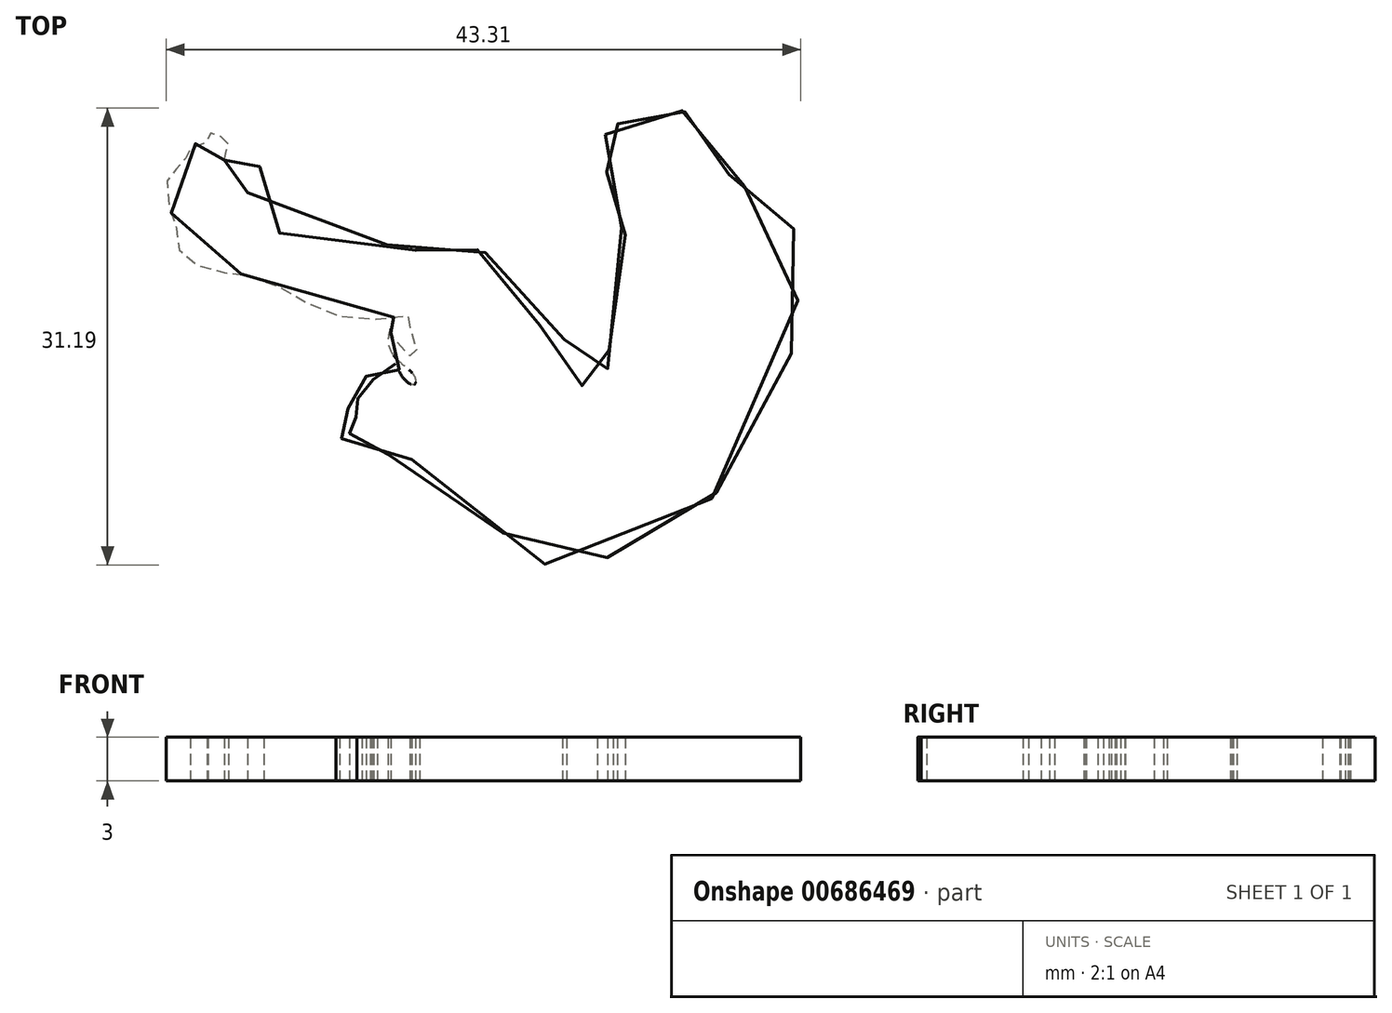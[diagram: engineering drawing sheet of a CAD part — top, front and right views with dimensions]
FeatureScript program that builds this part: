
annotation { "Feature Type Name" : "Feature", "Feature Type Description" : "" }
export const myFeature = defineFeature(function(context is Context, id is Id, definition is map)
    precondition{}
    {
        {
            var Q0;
            Q0=qCreatedBy(makeId("Top.planeOp"),FACE);
            var sketch = newSketch(context, id + "F0", { "sketchPlane" : qUnion([Q0])});
            skFitSpline(sketch, "E0", {"points": [v(-54, 35.11) * mm, v(-53.98, 35.18) * mm, v(-53.72, 36.26) * mm, v(-53.86, 36.83) * mm, v(-54.43, 36.67) * mm, v(-54.64, 36.97) * mm, v(-55.17, 36.79) * mm, v(-55.12, 36.37) * mm, v(-55.79, 36.33) * mm, v(-56.3, 35.82) * mm, v(-56.31, 35.57) * mm, v(-56.75, 35.18) * mm, v(-57.23, 34.63) * mm, v(-57.37, 34.34) * mm, v(-57.83, 33.88) * mm, v(-57.78, 31.98) * mm, v(-57.28, 30.6) * mm, v(-57.16, 29.25) * mm, v(-56.34, 28.2) * mm, v(-54.1, 27.46) * mm, v(-53.04, 27.37) * mm, v(-49.83, 26.27) * mm, v(-47.22, 24.8) * mm, v(-43.37, 24.28) * mm, v(-41.24, 24.44) * mm, v(-41.28, 23.91) * mm, v(-41.08, 22.51) * mm, v(-40.69, 21.67) * mm, v(-42.4, 22.51) * mm, v(-42.63, 23.61) * mm, v(-42.8, 22.6) * mm, v(-41.83, 21.18) * mm, v(-41, 20.34) * mm, v(-41.03, 19.79) * mm, v(-42, 20.59) * mm, v(-42.18, 21.32) * mm, v(-42.73, 21.02) * mm, v(-43.85, 21.57) * mm, v(-43.55, 20.68) * mm, v(-43.94, 20.95) * mm, v(-43.8, 20.2) * mm, v(-44.23, 20.33) * mm, v(-45.42, 20.45) * mm, v(-44.9, 19.52) * mm, v(-44.3, 18.99) * mm, v(-44.7, 18.84) * mm, v(-46.12, 18.91) * mm, v(-45.67, 18.3) * mm, v(-45.24, 17.97) * mm, v(-44.6, 17.86) * mm, v(-44.85, 17.66) * mm, v(-45.22, 17.39) * mm, v(-45.77, 16.81) * mm, v(-46.09, 16.8) * mm, v(-46.37, 16.42) * mm, v(-46.2, 15.89) * mm, v(-45.52, 16.46) * mm, v(-44.02, 15.62) * mm, v(-44.26, 15.42) * mm, v(-44.92, 14.7) * mm, v(-43.05, 15.02) * mm, v(-40.02, 13.98) * mm, v(-35.1, 9.77) * mm, v(-33.36, 8.2) * mm, v(-31.76, 7.49) * mm, v(-26.23, 8.02) * mm, v(-25.52, 7.7) * mm, v(-20.07, 12.82) * mm, v(-16.12, 19.16) * mm, v(-15.06, 23.56) * mm, v(-14.67, 29.52) * mm, v(-14.9, 30.13) * mm, v(-16.37, 31.9) * mm, v(-18.02, 33.26) * mm, v(-19.33, 33.64) * mm, v(-19.64, 35.14) * mm, v(-19.99, 36.5) * mm, v(-21.42, 37.92) * mm, v(-22.73, 38.5) * mm, v(-22.96, 38.61) * mm, v(-24.96, 38.57) * mm, v(-26.15, 38.07) * mm, v(-27.16, 37.57) * mm, v(-27.16, 37.3) * mm, v(-27.7, 36.84) * mm, v(-28.12, 36.88) * mm, v(-28.54, 36.18) * mm, v(-27.81, 34.07) * mm, v(-27.66, 32.76) * mm, v(-26.96, 31.56) * mm, v(-26.85, 30.44) * mm, v(-26.66, 30.13) * mm, v(-27.16, 26.94) * mm, v(-27.5, 23.66) * mm, v(-27.77, 20.46) * mm, v(-27.54, 19.11) * mm, v(-29.24, 18.96) * mm, v(-29.66, 19.92) * mm, v(-30.9, 22.12) * mm, v(-30.66, 23.55) * mm, v(-32.51, 23.9) * mm, v(-34.79, 27.2) * mm, v(-35.36, 28.2) * mm, v(-36.83, 29.02) * mm, v(-37.52, 28.82) * mm, v(-37.95, 29.06) * mm, v(-39.56, 29.21) * mm, v(-40.45, 28.94) * mm, v(-43.1, 29.36) * mm, v(-49.31, 29.9) * mm, v(-51.16, 30.67) * mm, v(-52.28, 32.22) * mm, v(-52.17, 33.87) * mm, v(-51.36, 35.07) * mm, v(-51.43, 36) * mm, v(-52.01, 36.26) * mm, v(-53.24, 35.6) * mm, v(-54, 35.11) * mm]});
            skSolve(sketch);
        }
        {
            var Q0;
            Q0 = qSketchRegion(id + "F0", true);
            extrude(context, id + "F1", {"entities" : qUnion([Q0]), "depth" : 3 * mm, "offsetDistance" : 25.4 * mm});
        }
    });
